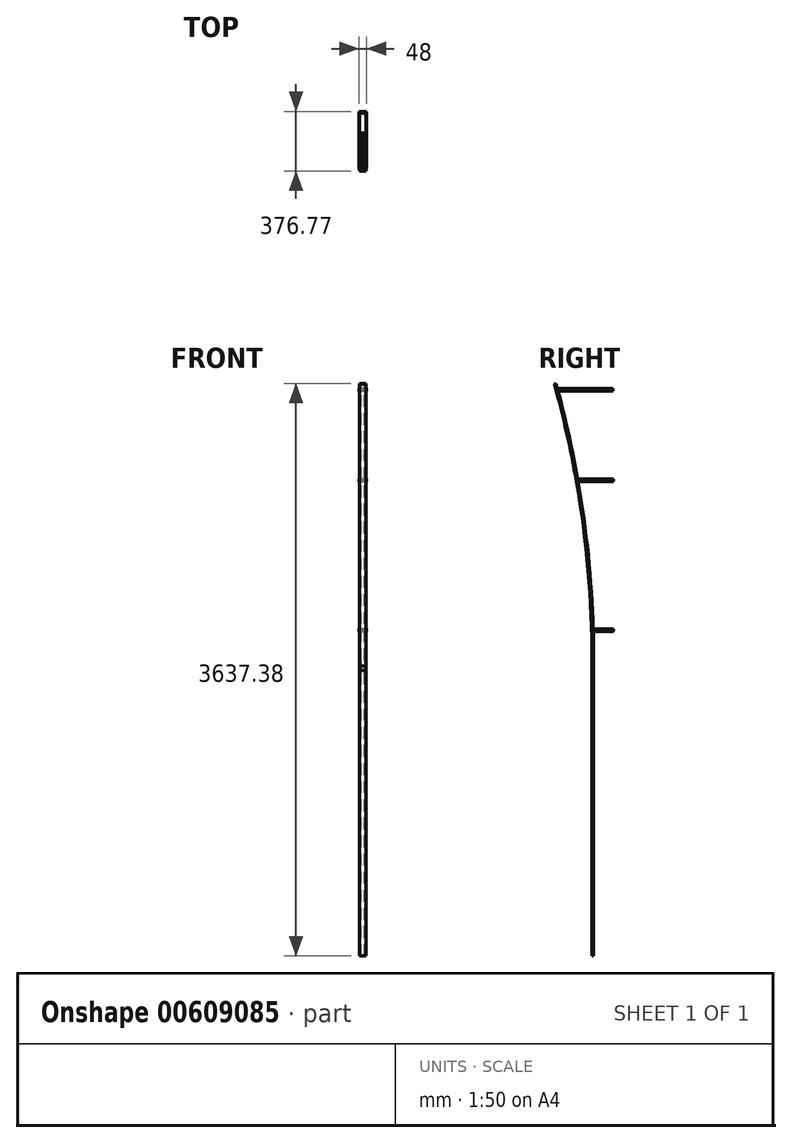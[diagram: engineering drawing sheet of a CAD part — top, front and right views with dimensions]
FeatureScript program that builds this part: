
annotation { "Feature Type Name" : "Feature", "Feature Type Description" : "" }
export const myFeature = defineFeature(function(context is Context, id is Id, definition is map)
    precondition{}
    {
        {
            var Q0;
            Q0=qCreatedBy(makeId("Top.planeOp"),FACE);
            var sketch = newSketch(context, id + "F0", { "sketchPlane" : qUnion([Q0])});
            skLineSegment(sketch, "E0.bottom", {"start": v(-18.5, 3.5) * mm, "end": v(18.5, 3.5) * mm});
            skLineSegment(sketch, "E0.top", {"start": v(-18.5, -3.5) * mm, "end": v(18.5, -3.5) * mm});
            skLineSegment(sketch, "E0.left", {"start": v(-18.5, 3.5) * mm, "end": v(-18.5, -3.5) * mm});
            skLineSegment(sketch, "E0.right", {"start": v(18.5, 3.5) * mm, "end": v(18.5, -3.5) * mm});
            skPoint(sketch, "E0.middle", {"position": v(0, 0) * mm});
            skLineSegment(sketch, "E1.bottom", {"start": v(-20, 5) * mm, "end": v(20, 5) * mm});
            skLineSegment(sketch, "E1.top", {"start": v(-20, -5) * mm, "end": v(20, -5) * mm});
            skLineSegment(sketch, "E1.left", {"start": v(-20, 5) * mm, "end": v(-20, -5) * mm});
            skLineSegment(sketch, "E1.right", {"start": v(20, 5) * mm, "end": v(20, -5) * mm});
            skLineSegment(sketch, "E2.bottom", {"start": v(-12.5, 0) * mm, "end": v(12.5, 0) * mm});
            skLineSegment(sketch, "E2.top", {"start": v(-12.5, 10) * mm, "end": v(12.5, 10) * mm});
            skLineSegment(sketch, "E2.left", {"start": v(-12.5, 0) * mm, "end": v(-12.5, 10) * mm});
            skLineSegment(sketch, "E2.right", {"start": v(12.5, 0) * mm, "end": v(12.5, 10) * mm});
            skPoint(sketch, "E2.middle", {"position": v(0, 5) * mm});
            skSolve(sketch);
        }
        {
            var Q0;
            Q0=makeQuery(id+"F0.imprint","IMPRINT",FACE,{"disambiguationData":[TD([[makeQuery(id+"F0.imprint","IMPRINT",EDGE,{"derivedFrom":sQuery(id+"F0.wireOp",EDGE,"E0.top")}),-1.0]])]});
            extrude(context, id + "F1", {"entities" : qUnion([Q0]), "oppositeDirection" : true, "depth" : 1828.8 * mm, "offsetDistance" : 25 * mm});
        }
        {
            var Q0;
            Q0=makeQuery(id+"F1.opExtrude","SWEPT_FACE",FACE,{"disambiguationData":[OSD([sQuery(id+"F0.wireOp",EDGE,"E0.top")])]});
            var sketch = newSketch(context, id + "F2", { "sketchPlane" : qUnion([Q0])});
            skCircle(sketch, "E3", {"center": v(0, 3.28) * mm, "radius": 18.79 * mm});
            skPoint(sketch, "E3.first.point", {"position": v(18.5, 0) * mm});
            skPoint(sketch, "E3.second.point", {"position": v(-18.5, 0) * mm});
            skPoint(sketch, "E3.third.point", {"position": v(-3.42, -15.2) * mm});
            skSolve(sketch);
        }
        {
            var Q0;
            {var subQ1=sQuery(id+"F0.wireOp",EDGE,"E0.top");var subQ2=makeQuery(id+"F1.opExtrude","CAP_EDGE",EDGE,{"disambiguationData":[OSD([subQ1])],"isStart":true});Q0=makeQuery(id+"F2.imprint","IMPRINT",FACE,{"disambiguationData":[TD([[makeQuery(id+"F2.imprint","IMPRINT",EDGE,{"derivedFrom":subQ2}),1.0]])]});}
            extrude(context, id + "F3", {"entities" : qUnion([Q0]), "operationType" : NewBodyOperationType.REMOVE, "endBound" : BoundingType.SYMMETRIC, "depth" : 25 * mm, "offsetDistance" : 25 * mm});
        }
        {
            var Q0;
            Q0=makeQuery(id+"F0.imprint","IMPRINT",FACE,{"disambiguationData":[TD([[makeQuery(id+"F0.imprint","IMPRINT",EDGE,{"derivedFrom":sQuery(id+"F0.wireOp",EDGE,"E0.top")}),-1.0]])]});
            extrude(context, id + "F4", {"entities" : qUnion([Q0]), "depth" : 50 * mm, "offsetDistance" : 25 * mm});
        }
        {
            var Q0;
            Q0=makeQuery(id+"F4.opExtrude","SWEPT_FACE",FACE,{"disambiguationData":[OSD([sQuery(id+"F0.wireOp",EDGE,"E1.right")])]});
            var sketch = newSketch(context, id + "F5", { "sketchPlane" : qUnion([Q0])});
            skArc(sketch, "E4", {"start": v(-5, 50) * mm, "mid": v(-65.04, 936.06) * mm, "end": v(-244.06, 1805.91) * mm});
            skSolve(sketch);
        }
        {
            var Q0;
            Q0=makeQuery(id+"F4.opExtrude","CAP_FACE",FACE,{"disambiguationData":[OSD([sQuery(id+"F0.wireOp",EDGE,"E0.bottom"),sQuery(id+"F0.wireOp",EDGE,"E0.top"),sQuery(id+"F0.wireOp",EDGE,"E0.left"),sQuery(id+"F0.wireOp",EDGE,"E0.right"),sQuery(id+"F0.wireOp",EDGE,"E1.bottom"),sQuery(id+"F0.wireOp",EDGE,"E1.top"),sQuery(id+"F0.wireOp",EDGE,"E1.left"),sQuery(id+"F0.wireOp",EDGE,"E1.right"),sQuery(id+"F0.wireOp",EDGE,"E2.left"),sQuery(id+"F0.wireOp",EDGE,"E2.right")])],"isStart":false});
            var Q1;
            Q1=sQuery(id+"F5.wireOp",EDGE,"E4");
            sweep(context, id + "F6", {"operationType" : NewBodyOperationType.ADD, "profiles" : qUnion([Q0]), "path" : qUnion([Q1])});
        }
        {
            var Q0;
            Q0=makeQuery(id+"F4.opExtrude","SWEPT_FACE",FACE,{"disambiguationData":[OSD([sQuery(id+"F0.wireOp",EDGE,"E1.top")])]});
            var sketch = newSketch(context, id + "F7", { "sketchPlane" : qUnion([Q0])});
            skArc(sketch, "E5", {"start": v(18.45, 0) * mm, "mid": v(0.05, 13.41) * mm, "end": v(-18.35, 0) * mm});
            skSolve(sketch);
        }
        {
            var Q0;
            {var subQ0=sQuery(id+"F7.wireOp",EDGE,"E5");Q0=makeQuery(id+"F7.imprint","IMPRINT",FACE,{"disambiguationData":[TD([[makeQuery(id+"F7.imprint","IMPRINT",EDGE,{"derivedFrom":subQ0}),1.0]])]});}
            extrude(context, id + "F8", {"entities" : qUnion([Q0]), "operationType" : NewBodyOperationType.REMOVE, "oppositeDirection" : true, "depth" : 25 * mm, "offsetDistance" : 25 * mm});
        }
        {
            var Q0;
            {var subQ0=sQuery(id+"F0.wireOp",EDGE,"E1.left");Q0=makeQuery(id+"F6.boolean.opBoolean","MERGE",FACE,{"derivedFrom":[makeQuery(id+"F4.opExtrude","SWEPT_FACE",FACE,{"disambiguationData":[OSD([subQ0])]}),makeQuery(id+"F6.opSweep","SWEPT_FACE",FACE,{"disambiguationData":[OSD([subQ0,sQuery(id+"F5.wireOp",EDGE,"E4")])]})]});}
            var sketch = newSketch(context, id + "F9", { "sketchPlane" : qUnion([Q0])});
            skLineSegment(sketch, "E6.bottom", {"start": v(7.7, 248.26) * mm, "end": v(-132.3, 248.26) * mm});
            skLineSegment(sketch, "E6.top", {"start": v(7.7, 233.26) * mm, "end": v(-132.3, 233.26) * mm});
            skLineSegment(sketch, "E6.left", {"start": v(7.7, 248.26) * mm, "end": v(7.7, 233.26) * mm});
            skLineSegment(sketch, "E6.right", {"start": v(-132.3, 248.26) * mm, "end": v(-132.3, 233.26) * mm});
            skLineSegment(sketch, "E7.bottom", {"start": v(96.26, 1199.75) * mm, "end": v(-132.7, 1199.75) * mm});
            skLineSegment(sketch, "E7.top", {"start": v(96.26, 1184.75) * mm, "end": v(-132.7, 1184.75) * mm});
            skLineSegment(sketch, "E7.left", {"start": v(96.26, 1199.75) * mm, "end": v(96.26, 1184.75) * mm});
            skLineSegment(sketch, "E7.right", {"start": v(-132.7, 1199.75) * mm, "end": v(-132.7, 1184.75) * mm});
            skLineSegment(sketch, "E8.bottom", {"start": v(-128.94, 1776.54) * mm, "end": v(231.92, 1776.54) * mm});
            skLineSegment(sketch, "E8.top", {"start": v(-128.94, 1761.54) * mm, "end": v(231.92, 1761.54) * mm});
            skLineSegment(sketch, "E8.left", {"start": v(-128.94, 1776.54) * mm, "end": v(-128.94, 1761.54) * mm});
            skLineSegment(sketch, "E8.right", {"start": v(231.92, 1776.54) * mm, "end": v(231.92, 1761.54) * mm});
            skLineSegment(sketch, "E9.bottom", {"start": v(96.26, 1184.75) * mm, "end": v(103.6, 1184.75) * mm});
            skLineSegment(sketch, "E9.top", {"start": v(96.26, 1199.75) * mm, "end": v(103.6, 1199.75) * mm});
            skLineSegment(sketch, "E9.left", {"start": v(96.26, 1184.75) * mm, "end": v(96.26, 1199.75) * mm});
            skLineSegment(sketch, "E9.right", {"start": v(103.6, 1184.75) * mm, "end": v(103.6, 1199.75) * mm});
            skSolve(sketch);
        }
        {
            var Q0;
            {var subQ0=sQuery(id+"F9.wireOp",EDGE,"E6.right");Q0=makeQuery(id+"F9.imprint","IMPRINT",FACE,{"disambiguationData":[TD([[makeQuery(id+"F9.imprint","IMPRINT",EDGE,{"derivedFrom":subQ0}),1.0]])]});}
            var Q1;
            {var subQ0=sQuery(id+"F9.wireOp",EDGE,"E7.bottom");Q1=makeQuery(id+"F9.imprint","IMPRINT",FACE,{"disambiguationData":[TD([[makeQuery(id+"F9.imprint","IMPRINT",EDGE,{"derivedFrom":subQ0}),1.0]])]});}
            var Q2;
            {var subQ0=sQuery(id+"F9.wireOp",EDGE,"E8.left");Q2=makeQuery(id+"F9.imprint","IMPRINT",FACE,{"disambiguationData":[TD([[makeQuery(id+"F9.imprint","IMPRINT",EDGE,{"derivedFrom":subQ0}),1.0]])]});}
            var Q3;
            {var subQ5=sQuery(id+"F9.wireOp",EDGE,"E6.left");var subQ9=sQuery(id+"F9.wireOp",EDGE,"E6.bottom");var subQ10=makeQuery(id+"F9.imprint","INTERSECT",VERTEX,{"derivedFrom":[subQ9,subQ5]});Q3=makeQuery(id+"F9.imprint","IMPRINT",FACE,{"disambiguationData":[TD([[makeQuery(id+"F9.imprint","IMPRINT",EDGE,{"disambiguationData":[TD([[subQ10,-1.0]])],"derivedFrom":subQ9}),1.0]])]});}
            var Q4;
            {var subQ0=sQuery(id+"F9.wireOp",EDGE,"E7.left");Q4=makeQuery(id+"F9.imprint","IMPRINT",FACE,{"disambiguationData":[TD([[makeQuery(id+"F9.imprint","IMPRINT",EDGE,{"derivedFrom":subQ0}),-1.0]])]});}
            var Q5;
            {var subQ0=sQuery(id+"F9.wireOp",EDGE,"E8.right");Q5=makeQuery(id+"F9.imprint","IMPRINT",FACE,{"disambiguationData":[TD([[makeQuery(id+"F9.imprint","IMPRINT",EDGE,{"derivedFrom":subQ0}),-1.0]])]});}
            var Q6;
            Q6=makeQuery(id+"F9.imprint","IMPRINT",FACE,{"disambiguationData":[TD([[makeQuery(id+"F9.imprint","IMPRINT",EDGE,{"derivedFrom":sQuery(id+"F9.wireOp",EDGE,"E9.bottom")}),1.0]])]});
            var Q7;
            {var subQ0=sQuery(id+"F9.wireOp",EDGE,"E9.left");Q7=makeQuery(id+"F9.imprint","IMPRINT",FACE,{"disambiguationData":[TD([[makeQuery(id+"F9.imprint","IMPRINT",EDGE,{"derivedFrom":subQ0}),1.0]])]});}
            extrude(context, id + "F10", {"entities" : qUnion([Q0, Q1, Q2, Q3, Q4, Q5, Q6, Q7]), "operationType" : NewBodyOperationType.ADD, "depth" : 4 * mm, "offsetDistance" : 25 * mm});
        }
        {
            var Q0;
            Q0=makeQuery(id+"F10.opExtrude","CAP_FACE",FACE,{"disambiguationData":[OSD([sQuery(id+"F9.wireOp",EDGE,"E8.bottom"),sQuery(id+"F9.wireOp",EDGE,"E8.top"),sQuery(id+"F9.wireOp",EDGE,"E8.left"),sQuery(id+"F9.wireOp",EDGE,"E8.right")])],"isStart":true});
            var sketch = newSketch(context, id + "F11", { "sketchPlane" : qUnion([Q0])});
            skLineSegment(sketch, "E10.bottom", {"start": v(128.94, 1776.54) * mm, "end": v(123.94, 1776.54) * mm});
            skLineSegment(sketch, "E10.top", {"start": v(128.94, 1761.54) * mm, "end": v(123.94, 1761.54) * mm});
            skLineSegment(sketch, "E10.left", {"start": v(128.94, 1776.54) * mm, "end": v(128.94, 1761.54) * mm});
            skLineSegment(sketch, "E10.right", {"start": v(123.94, 1776.54) * mm, "end": v(123.94, 1761.54) * mm});
            skLineSegment(sketch, "E11.bottom", {"start": v(132.7, 1199.75) * mm, "end": v(127.7, 1199.75) * mm});
            skLineSegment(sketch, "E11.top", {"start": v(132.7, 1184.75) * mm, "end": v(127.7, 1184.75) * mm});
            skLineSegment(sketch, "E11.left", {"start": v(132.7, 1199.75) * mm, "end": v(132.7, 1184.75) * mm});
            skLineSegment(sketch, "E11.right", {"start": v(127.7, 1199.75) * mm, "end": v(127.7, 1184.75) * mm});
            skLineSegment(sketch, "E12.bottom", {"start": v(132.3, 233.26) * mm, "end": v(127.3, 233.26) * mm});
            skLineSegment(sketch, "E12.top", {"start": v(132.3, 248.26) * mm, "end": v(127.3, 248.26) * mm});
            skLineSegment(sketch, "E12.left", {"start": v(132.3, 233.26) * mm, "end": v(132.3, 248.26) * mm});
            skLineSegment(sketch, "E12.right", {"start": v(127.3, 233.26) * mm, "end": v(127.3, 248.26) * mm});
            skSolve(sketch);
        }
        {
            var Q0;
            Q0=makeQuery(id+"F11.imprint","IMPRINT",FACE,{"disambiguationData":[TD([[makeQuery(id+"F11.imprint","IMPRINT",EDGE,{"derivedFrom":sQuery(id+"F11.wireOp",EDGE,"E12.bottom")}),-1.0]])]});
            var Q1;
            Q1=makeQuery(id+"F11.imprint","IMPRINT",FACE,{"disambiguationData":[TD([[makeQuery(id+"F11.imprint","IMPRINT",EDGE,{"derivedFrom":sQuery(id+"F11.wireOp",EDGE,"E11.bottom")}),1.0]])]});
            var Q2;
            Q2=makeQuery(id+"F11.imprint","IMPRINT",FACE,{"disambiguationData":[TD([[makeQuery(id+"F11.imprint","IMPRINT",EDGE,{"derivedFrom":sQuery(id+"F11.wireOp",EDGE,"E10.bottom")}),1.0]])]});
            extrude(context, id + "F12", {"entities" : qUnion([Q0, Q1, Q2]), "operationType" : NewBodyOperationType.ADD, "depth" : 44 * mm, "offsetDistance" : 25 * mm});
        }
        {
            var Q0;
            Q0=makeQuery(id+"F12.opExtrude","SWEPT_FACE",FACE,{"disambiguationData":[OSD([sQuery(id+"F11.wireOp",EDGE,"E10.right")])]});
            var sketch = newSketch(context, id + "F13", { "sketchPlane" : qUnion([Q0])});
            skLineSegment(sketch, "E13", {"start": v(20, 1776.54) * mm, "end": v(20, 1761.54) * mm});
            skSolve(sketch);
        }
        {
            var Q0;
            {var subQ0=sQuery(id+"F13.wireOp",EDGE,"E13");Q0=makeQuery(id+"F13.imprint","IMPRINT",FACE,{"disambiguationData":[TD([[makeQuery(id+"F13.imprint","IMPRINT",EDGE,{"derivedFrom":subQ0}),1.0]])]});}
            extrude(context, id + "F14", {"entities" : qUnion([Q0]), "operationType" : NewBodyOperationType.ADD, "depth" : 354 * mm, "offsetDistance" : 25 * mm});
        }
        {
            var Q0;
            Q0=makeQuery(id+"F12.opExtrude","SWEPT_FACE",FACE,{"disambiguationData":[OSD([sQuery(id+"F11.wireOp",EDGE,"E12.right")])]});
            var sketch = newSketch(context, id + "F15", { "sketchPlane" : qUnion([Q0])});
            skLineSegment(sketch, "E14", {"start": v(20, 248.26) * mm, "end": v(20, 233.26) * mm});
            skSolve(sketch);
        }
        {
            var Q0;
            {var subQ0=sQuery(id+"F15.wireOp",EDGE,"E14");Q0=makeQuery(id+"F15.imprint","IMPRINT",FACE,{"disambiguationData":[TD([[makeQuery(id+"F15.imprint","IMPRINT",EDGE,{"derivedFrom":subQ0}),1.0]])]});}
            extrude(context, id + "F16", {"entities" : qUnion([Q0]), "operationType" : NewBodyOperationType.ADD, "depth" : 134.7 * mm, "offsetDistance" : 25 * mm});
        }
        {
            var Q0;
            Q0=makeQuery(id+"F12.opExtrude","SWEPT_FACE",FACE,{"disambiguationData":[OSD([sQuery(id+"F11.wireOp",EDGE,"E11.right")])]});
            var sketch = newSketch(context, id + "F17", { "sketchPlane" : qUnion([Q0])});
            skLineSegment(sketch, "E15", {"start": v(20, 1199.75) * mm, "end": v(20, 1184.75) * mm});
            skSolve(sketch);
        }
        {
            var Q0;
            {var subQ0=sQuery(id+"F17.wireOp",EDGE,"E15");Q0=makeQuery(id+"F17.imprint","IMPRINT",FACE,{"disambiguationData":[TD([[makeQuery(id+"F17.imprint","IMPRINT",EDGE,{"derivedFrom":subQ0}),1.0]])]});}
            extrude(context, id + "F18", {"entities" : qUnion([Q0]), "operationType" : NewBodyOperationType.ADD, "depth" : 231.5 * mm, "offsetDistance" : 25 * mm});
        }
    });
